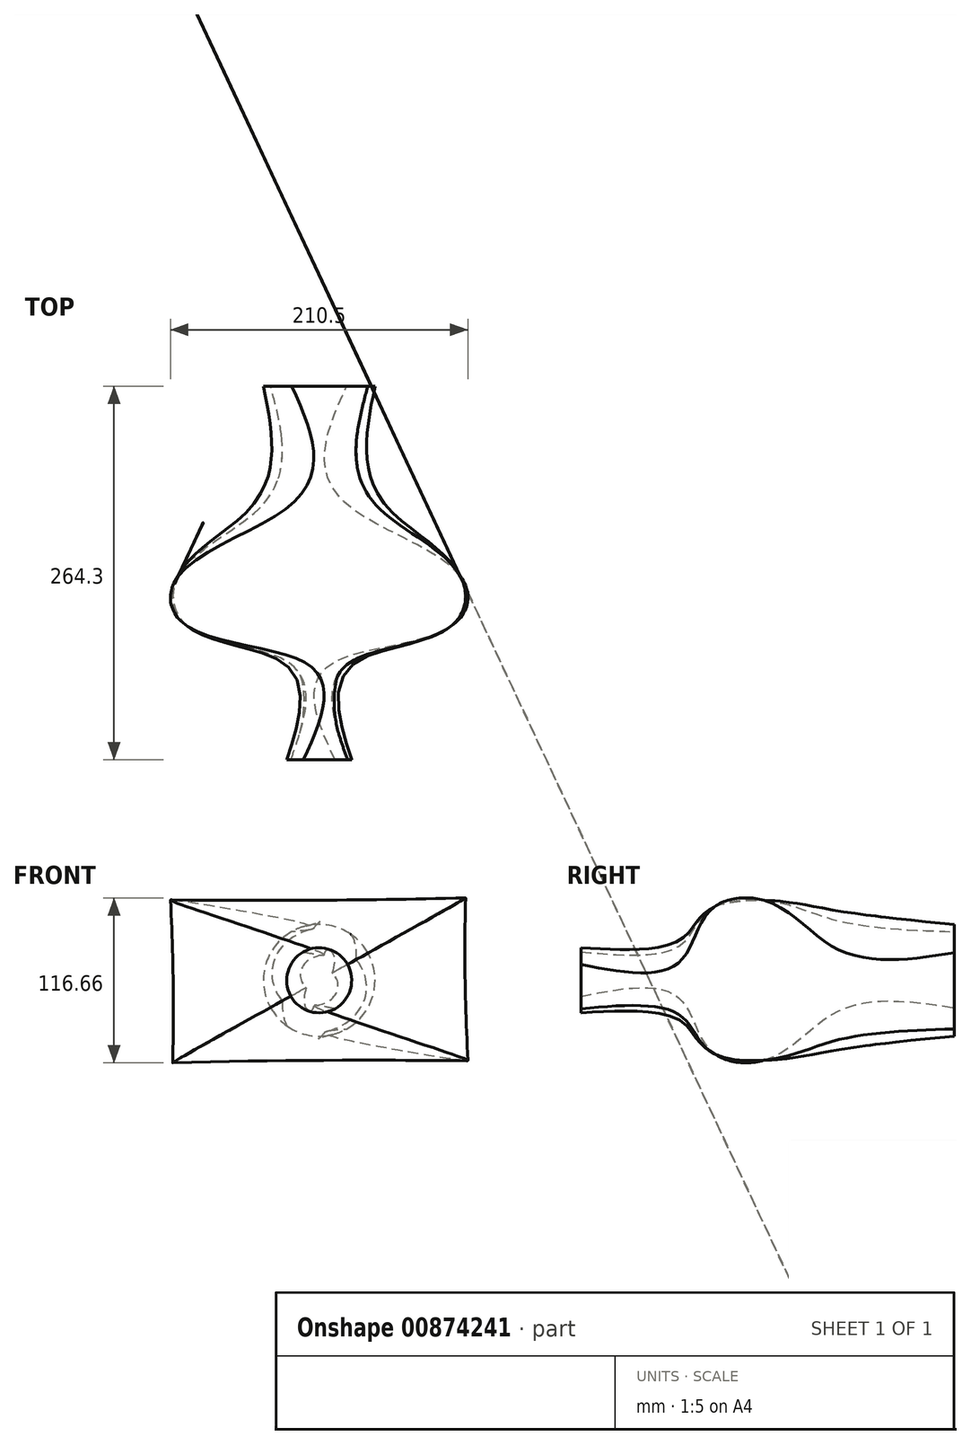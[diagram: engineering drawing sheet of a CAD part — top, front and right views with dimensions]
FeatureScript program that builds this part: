
annotation { "Feature Type Name" : "Feature", "Feature Type Description" : "" }
export const myFeature = defineFeature(function(context is Context, id is Id, definition is map)
    precondition{}
    {
        {
            var Q0;
            Q0=qCreatedBy(makeId("Front.planeOp"),FACE);
            cPlane(context, id + "F0", {"entities" : qUnion([Q0]), "cplaneType" : CPlaneType.OFFSET, "offset" : 87.5 * mm, "oppositeDirection" : true, "width" : 150 * mm, "height" : 150 * mm});
        }
        {
            var Q0;
            Q0=qCreatedBy(makeId("Front.planeOp"),FACE);
            var sketch = newSketch(context, id + "F1", { "sketchPlane" : qUnion([Q0])});
            skCircle(sketch, "E0", {"center": v(0, 0) * mm, "radius": 50 * mm});
            skSolve(sketch);
        }
        {
            var Q0;
            Q0=qCreatedBy(id+"F0.planeOp",FACE);
            var sketch = newSketch(context, id + "F2", { "sketchPlane" : qUnion([Q0])});
            skCircle(sketch, "E1", {"center": v(0, 0) * mm, "radius": 39.5 * mm});
            skSolve(sketch);
        }
        {
            var Q0;
            Q0=qCreatedBy(makeId("Front.planeOp"),FACE);
            cPlane(context, id + "F3", {"entities" : qUnion([Q0]), "cplaneType" : CPlaneType.OFFSET, "offset" : 47.1 * mm, "width" : 150 * mm, "height" : 150 * mm});
        }
        {
            var Q0;
            Q0=qCreatedBy(id+"F3.planeOp",FACE);
            var sketch = newSketch(context, id + "F4", { "sketchPlane" : qUnion([Q0])});
            skLineSegment(sketch, "E2.bottom", {"start": v(100, 56.5) * mm, "end": v(-100, 56.5) * mm});
            skLineSegment(sketch, "E2.top", {"start": v(100, -56.5) * mm, "end": v(-100, -56.5) * mm});
            skLineSegment(sketch, "E2.left", {"start": v(100, 56.5) * mm, "end": v(100, -56.5) * mm});
            skLineSegment(sketch, "E2.right", {"start": v(-100, 56.5) * mm, "end": v(-100, -56.5) * mm});
            skPoint(sketch, "E2.middle", {"position": v(0, 0) * mm});
            skSolve(sketch);
        }
        {
            var Q0;
            Q0=qCreatedBy(id+"F3.planeOp",FACE);
            cPlane(context, id + "F5", {"entities" : qUnion([Q0]), "cplaneType" : CPlaneType.OFFSET, "offset" : 58.7 * mm, "width" : 150 * mm, "height" : 150 * mm});
        }
        {
            var Q0;
            Q0=qCreatedBy(id+"F5.planeOp",FACE);
            var sketch = newSketch(context, id + "F6", { "sketchPlane" : qUnion([Q0])});
            skCircle(sketch, "E3", {"center": v(0, 0) * mm, "radius": 29 * mm});
            skSolve(sketch);
        }
        {
            var Q0;
            Q0=qCreatedBy(id+"F5.planeOp",FACE);
            cPlane(context, id + "F7", {"entities" : qUnion([Q0]), "cplaneType" : CPlaneType.OFFSET, "offset" : 71 * mm, "width" : 150 * mm, "height" : 150 * mm});
        }
        {
            var Q0;
            Q0=qCreatedBy(id+"F7.planeOp",FACE);
            var sketch = newSketch(context, id + "F8", { "sketchPlane" : qUnion([Q0])});
            skCircle(sketch, "E4", {"center": v(0, 0) * mm, "radius": 23 * mm});
            skSolve(sketch);
        }
        {
            var Q0;
            Q0=qCreatedBy(id+"F3.planeOp",FACE);
            cPlane(context, id + "F9", {"entities" : qUnion([Q0]), "cplaneType" : CPlaneType.OFFSET, "offset" : 35.3 * mm, "width" : 150 * mm, "height" : 150 * mm});
        }
        {
            var Q0;
            Q0=qCreatedBy(id+"F9.planeOp",FACE);
            var sketch = newSketch(context, id + "F10", { "sketchPlane" : qUnion([Q0])});
            skLineSegment(sketch, "E5.bottom", {"start": v(92.98, 51.92) * mm, "end": v(-92.98, 51.92) * mm});
            skLineSegment(sketch, "E5.top", {"start": v(92.98, -51.92) * mm, "end": v(-92.98, -51.92) * mm});
            skLineSegment(sketch, "E5.left", {"start": v(92.98, 51.92) * mm, "end": v(92.98, -51.92) * mm});
            skLineSegment(sketch, "E5.right", {"start": v(-92.98, 51.92) * mm, "end": v(-92.98, -51.92) * mm});
            skPoint(sketch, "E5.middle", {"position": v(0, 0) * mm});
            skSolve(sketch);
        }
        {
            var Q0;
            Q0=makeQuery(id+"F8.imprint","IMPRINT",FACE,{"disambiguationData":[TD([[makeQuery(id+"F8.imprint","IMPRINT",EDGE,{"derivedFrom":sQuery(id+"F8.wireOp",EDGE,"E4")}),1.0]])]});
            var Q1;
            Q1=makeQuery(id+"F6.imprint","IMPRINT",FACE,{"disambiguationData":[TD([[makeQuery(id+"F6.imprint","IMPRINT",EDGE,{"derivedFrom":sQuery(id+"F6.wireOp",EDGE,"E3")}),1.0]])]});
            var Q2;
            Q2=makeQuery(id+"F10.imprint","IMPRINT",FACE,{"disambiguationData":[TD([[makeQuery(id+"F10.imprint","IMPRINT",EDGE,{"derivedFrom":sQuery(id+"F10.wireOp",EDGE,"E5.bottom")}),1.0]])]});
            var Q3;
            Q3=makeQuery(id+"F4.imprint","IMPRINT",FACE,{"disambiguationData":[TD([[makeQuery(id+"F4.imprint","IMPRINT",EDGE,{"derivedFrom":sQuery(id+"F4.wireOp",EDGE,"E2.bottom")}),1.0]])]});
            var Q4;
            Q4=makeQuery(id+"F1.imprint","IMPRINT",FACE,{"disambiguationData":[TD([[makeQuery(id+"F1.imprint","IMPRINT",EDGE,{"derivedFrom":sQuery(id+"F1.wireOp",EDGE,"E0")}),1.0]])]});
            var Q5;
            Q5=makeQuery(id+"F2.imprint","IMPRINT",FACE,{"disambiguationData":[TD([[makeQuery(id+"F2.imprint","IMPRINT",EDGE,{"derivedFrom":sQuery(id+"F2.wireOp",EDGE,"E1")}),1.0]])]});
            loft(context, id + "F11", {"sheetProfilesArray" : [{ "sheetProfileEntities" : qUnion([Q0]) }, { "sheetProfileEntities" : qUnion([Q1]) }, { "sheetProfileEntities" : qUnion([Q2]) }, { "sheetProfileEntities" : qUnion([Q3]) }, { "sheetProfileEntities" : qUnion([Q4]) }, { "sheetProfileEntities" : qUnion([Q5]) }]});
        }
    });
